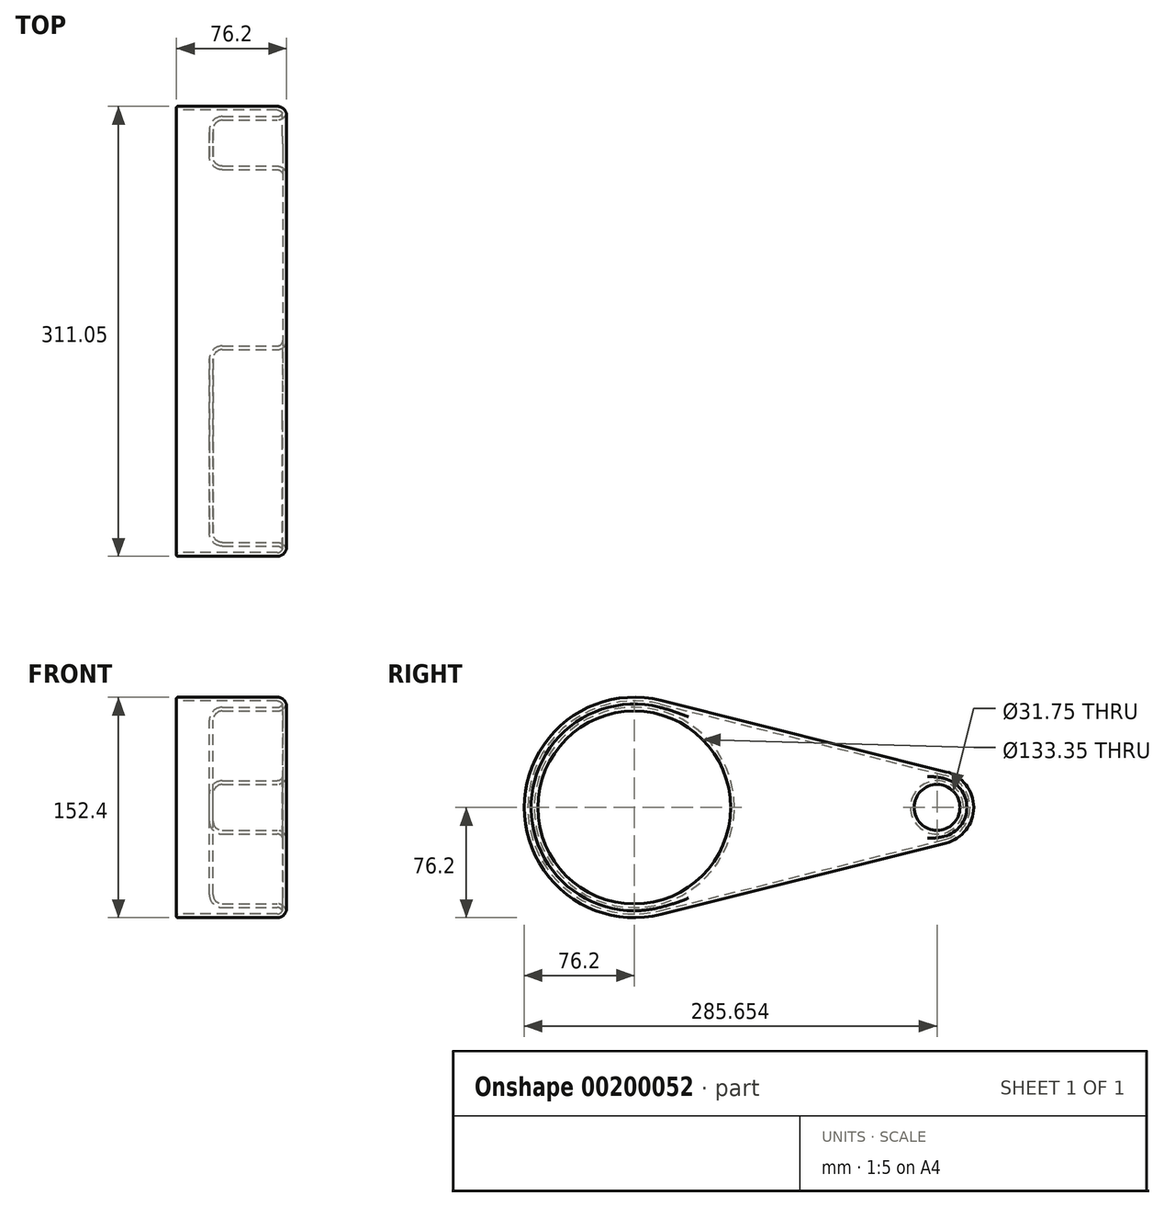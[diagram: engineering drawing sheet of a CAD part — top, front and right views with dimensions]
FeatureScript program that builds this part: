
annotation { "Feature Type Name" : "Feature", "Feature Type Description" : "" }
export const myFeature = defineFeature(function(context is Context, id is Id, definition is map)
    precondition{}
    {
        {
            var Q0;
            Q0=qCreatedBy(makeId("Right.planeOp"),FACE);
            var sketch = newSketch(context, id + "F0", { "sketchPlane" : qUnion([Q0])});
            skCircle(sketch, "E0", {"center": v(0, 0) * mm, "radius": 76.2 * mm});
            skCircle(sketch, "E1", {"center": v(209.45, 0) * mm, "radius": 25.4 * mm});
            skLineSegment(sketch, "E2", {"start": v(18.48, 73.92) * mm, "end": v(215.61, 24.64) * mm});
            skLineSegment(sketch, "E3", {"start": v(18.48, -73.92) * mm, "end": v(215.61, -24.64) * mm});
            skSolve(sketch);
        }
        {
            var Q0;
            {var subQ0=sQuery(id+"F0.wireOp",EDGE,"E0");var subQ1=makeQuery(id+"F0.imprint","INTERSECT",VERTEX,{"derivedFrom":[subQ0,sQuery(id+"F0.wireOp",EDGE,"E2")]});Q0=makeQuery(id+"F0.imprint","IMPRINT",FACE,{"disambiguationData":[TD([[makeQuery(id+"F0.imprint","IMPRINT",EDGE,{"disambiguationData":[TD([[subQ1,-1.0]])],"derivedFrom":subQ0}),1.0]])]});}
            var Q1;
            {var subQ0=sQuery(id+"F0.wireOp",EDGE,"E2");Q1=makeQuery(id+"F0.imprint","IMPRINT",FACE,{"disambiguationData":[TD([[makeQuery(id+"F0.imprint","IMPRINT",EDGE,{"derivedFrom":subQ0}),-1.0]])]});}
            var Q2;
            {var subQ0=sQuery(id+"F0.wireOp",EDGE,"E1");var subQ1=makeQuery(id+"F0.imprint","INTERSECT",VERTEX,{"derivedFrom":[subQ0,sQuery(id+"F0.wireOp",EDGE,"E2")]});Q2=makeQuery(id+"F0.imprint","IMPRINT",FACE,{"disambiguationData":[TD([[makeQuery(id+"F0.imprint","IMPRINT",EDGE,{"disambiguationData":[TD([[subQ1,-1.0]])],"derivedFrom":subQ0}),1.0]])]});}
            extrude(context, id + "F1", {"entities" : qUnion([Q0, Q1, Q2]), "depth" : 76.2 * mm});
        }
        {
            var Q0;
            Q0=makeQuery(id+"F1.opExtrude","CAP_FACE",FACE,{"disambiguationData":[OSD([sQuery(id+"F0.wireOp",EDGE,"E0"),sQuery(id+"F0.wireOp",EDGE,"E1"),sQuery(id+"F0.wireOp",EDGE,"E2"),sQuery(id+"F0.wireOp",EDGE,"E3")])],"isStart":false});
            var sketch = newSketch(context, id + "F2", { "sketchPlane" : qUnion([Q0])});
            skCircle(sketch, "E4", {"center": v(0, 0) * mm, "radius": 66.68 * mm});
            skCircle(sketch, "E5", {"center": v(209.45, 0) * mm, "radius": 15.88 * mm});
            skSolve(sketch);
        }
        {
            var Q0;
            Q0=makeQuery(id+"F2.imprint","IMPRINT",FACE,{"disambiguationData":[TD([[makeQuery(id+"F2.imprint","IMPRINT",EDGE,{"derivedFrom":sQuery(id+"F2.wireOp",EDGE,"E4")}),1.0]])]});
            var Q1;
            Q1=makeQuery(id+"F2.imprint","IMPRINT",FACE,{"disambiguationData":[TD([[makeQuery(id+"F2.imprint","IMPRINT",EDGE,{"derivedFrom":sQuery(id+"F2.wireOp",EDGE,"E5")}),1.0]])]});
            extrude(context, id + "F3", {"entities" : qUnion([Q0, Q1]), "operationType" : NewBodyOperationType.REMOVE, "oppositeDirection" : true, "depth" : 50.8 * mm});
        }
        {
            var Q0;
            Q0=makeQuery(id+"F1.opExtrude","CAP_FACE",FACE,{"disambiguationData":[OSD([sQuery(id+"F0.wireOp",EDGE,"E0"),sQuery(id+"F0.wireOp",EDGE,"E1"),sQuery(id+"F0.wireOp",EDGE,"E2"),sQuery(id+"F0.wireOp",EDGE,"E3")])],"isStart":false});
            var Q1;
            Q1=makeQuery(id+"F3.boolean.opBoolean","COPY",EDGE,{"derivedFrom":makeQuery(id+"F3.opExtrude","CAP_EDGE",EDGE,{"disambiguationData":[OSD([sQuery(id+"F2.wireOp",EDGE,"E4")])],"isStart":false})});
            var Q2;
            Q2=makeQuery(id+"F3.boolean.opBoolean","COPY",EDGE,{"derivedFrom":makeQuery(id+"F3.opExtrude","CAP_EDGE",EDGE,{"disambiguationData":[OSD([sQuery(id+"F2.wireOp",EDGE,"E5")])],"isStart":false})});
            fillet(context, id + "F4", {"entities" : qUnion([Q0, Q1, Q2]), "radius" : 6.35 * mm, "tangentPropagation" : true, "allowEdgeOverflow" : false});
        }
        {
            var Q0;
            Q0=makeQuery(id+"F1.opExtrude","CAP_FACE",FACE,{"disambiguationData":[OSD([sQuery(id+"F0.wireOp",EDGE,"E0"),sQuery(id+"F0.wireOp",EDGE,"E1"),sQuery(id+"F0.wireOp",EDGE,"E2"),sQuery(id+"F0.wireOp",EDGE,"E3")])],"isStart":true});
            shell(context, id + "F5", {"entities" : qUnion([Q0]), "thickness" : 2.54 * mm});
        }
        {
            var Q0;
            Q0=makeQuery(id+"F1.opExtrude","CAP_EDGE",EDGE,{"disambiguationData":[OSD([sQuery(id+"F0.wireOp",EDGE,"E3")])],"isStart":true});
            var Q1;
            {var subQ0=sQuery(id+"F0.wireOp",EDGE,"E3");Q1=makeQuery(id+"F5.opShell","OFFSET_EDGE",EDGE,{"disambiguationData":[OSD([subQ0]),TDD([makeQuery(id+"F1.opExtrude","CAP_EDGE",EDGE,{"disambiguationData":[OSD([subQ0])],"isStart":true})])]});}
            var Q2;
            Q2=makeQuery(id+"F1.opExtrude","CAP_EDGE",EDGE,{"disambiguationData":[OSD([sQuery(id+"F0.wireOp",EDGE,"E0")])],"isStart":true});
            var Q3;
            {var subQ0=sQuery(id+"F0.wireOp",EDGE,"E0");Q3=makeQuery(id+"F5.opShell","OFFSET_EDGE",EDGE,{"disambiguationData":[OSD([subQ0]),TDD([makeQuery(id+"F1.opExtrude","CAP_EDGE",EDGE,{"disambiguationData":[OSD([subQ0])],"isStart":true})])]});}
            var Q4;
            {var subQ0=sQuery(id+"F0.wireOp",EDGE,"E2");Q4=makeQuery(id+"F5.opShell","OFFSET_EDGE",EDGE,{"disambiguationData":[OSD([subQ0]),TDD([makeQuery(id+"F1.opExtrude","CAP_EDGE",EDGE,{"disambiguationData":[OSD([subQ0])],"isStart":true})])]});}
            var Q5;
            Q5=makeQuery(id+"F1.opExtrude","CAP_EDGE",EDGE,{"disambiguationData":[OSD([sQuery(id+"F0.wireOp",EDGE,"E2")])],"isStart":true});
            var Q6;
            {var subQ0=sQuery(id+"F0.wireOp",EDGE,"E1");Q6=makeQuery(id+"F5.opShell","OFFSET_EDGE",EDGE,{"disambiguationData":[OSD([subQ0]),TDD([makeQuery(id+"F1.opExtrude","CAP_EDGE",EDGE,{"disambiguationData":[OSD([subQ0])],"isStart":true})])]});}
            var Q7;
            Q7=makeQuery(id+"F1.opExtrude","CAP_EDGE",EDGE,{"disambiguationData":[OSD([sQuery(id+"F0.wireOp",EDGE,"E1")])],"isStart":true});
            fillet(context, id + "F6", {"entities" : qUnion([Q0, Q1, Q2, Q3, Q4, Q5, Q6, Q7]), "radius" : 1 * mm, "tangentPropagation" : true, "allowEdgeOverflow" : false});
        }
    });
